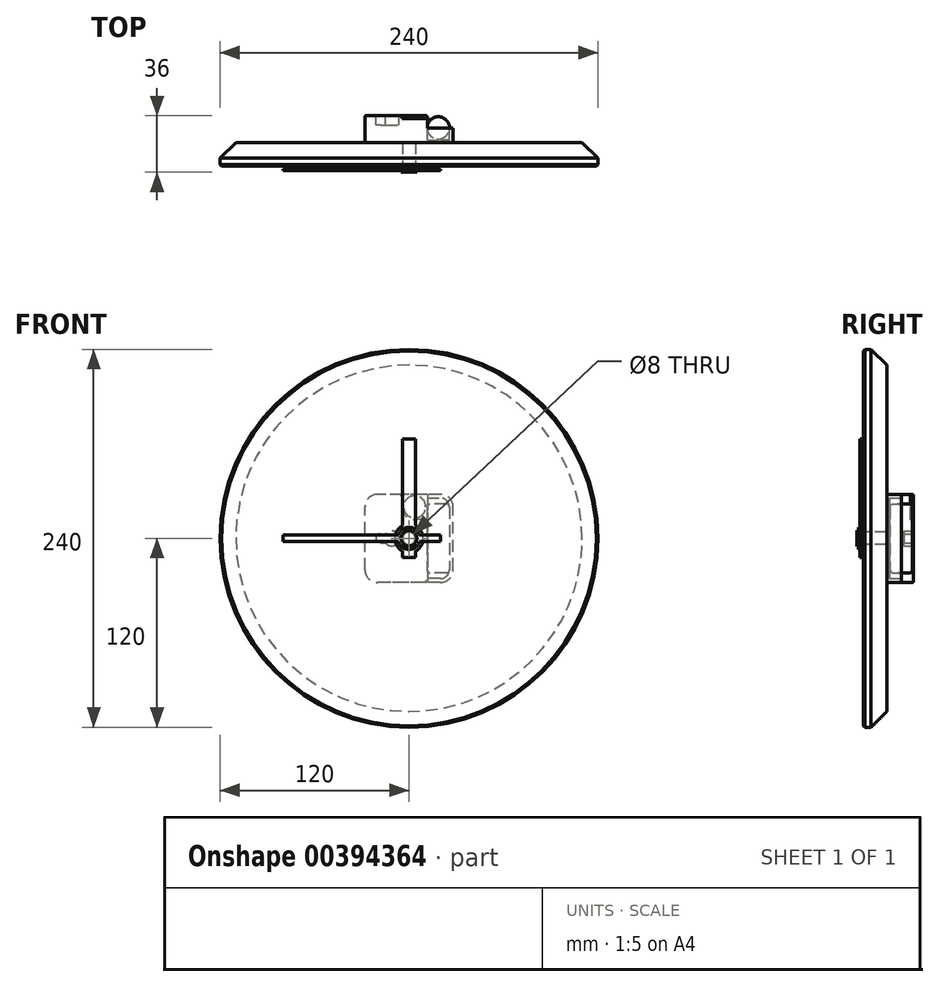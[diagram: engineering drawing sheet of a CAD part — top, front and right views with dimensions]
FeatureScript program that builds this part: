
annotation { "Feature Type Name" : "Feature", "Feature Type Description" : "" }
export const myFeature = defineFeature(function(context is Context, id is Id, definition is map)
    precondition{}
    {
        {
            var Q0;
            Q0=qCreatedBy(makeId("Front.planeOp"),FACE);
            var sketch = newSketch(context, id + "F0", { "sketchPlane" : qUnion([Q0])});
            skCircle(sketch, "E0", {"center": v(0, 0) * mm, "radius": 120 * mm});
            skSolve(sketch);
        }
        {
            var Q0;
            Q0=makeQuery(id+"F0.imprint","IMPRINT",FACE,{"disambiguationData":[TD([[makeQuery(id+"F0.imprint","IMPRINT",EDGE,{"derivedFrom":sQuery(id+"F0.wireOp",EDGE,"E0")}),1.0]])]});
            extrude(context, id + "F1", {"entities" : qUnion([Q0]), "oppositeDirection" : true, "depth" : 15 * mm});
        }
        {
            var Q0;
            Q0=makeQuery(id+"F1.opExtrude","CAP_FACE",FACE,{"disambiguationData":[OSD([sQuery(id+"F0.wireOp",EDGE,"E0")])],"isStart":false});
            var sketch = newSketch(context, id + "F2", { "sketchPlane" : qUnion([Q0])});
            skCircle(sketch, "E1", {"center": v(0, 0) * mm, "radius": 2.5 * mm});
            skSolve(sketch);
        }
        {
            var Q0;
            Q0=makeQuery(id+"F2.imprint","IMPRINT",FACE,{"disambiguationData":[TD([[makeQuery(id+"F2.imprint","IMPRINT",EDGE,{"derivedFrom":sQuery(id+"F2.wireOp",EDGE,"E1")}),1.0]])]});
            var Q1;
            Q1=makeQuery(id+"F1.opExtrude","CAP_FACE",FACE,{"disambiguationData":[OSD([sQuery(id+"F0.wireOp",EDGE,"E0")])],"isStart":true});
            extrude(context, id + "F3", {"entities" : qUnion([Q0]), "operationType" : NewBodyOperationType.REMOVE, "endBound" : BoundingType.UP_TO_SURFACE, "oppositeDirection" : true, "endBoundEntityFace" : qUnion([Q1]), "depth" : 20 * mm});
        }
        {
            var Q0;
            Q0=makeQuery(id+"F1.opExtrude","CAP_FACE",FACE,{"disambiguationData":[OSD([sQuery(id+"F0.wireOp",EDGE,"E0")])],"isStart":false});
            var sketch = newSketch(context, id + "F4", { "sketchPlane" : qUnion([Q0])});
            skLineSegment(sketch, "E2.bottom", {"start": v(-20, -28) * mm, "end": v(20, -28) * mm});
            skLineSegment(sketch, "E2.top", {"start": v(-20, 28) * mm, "end": v(20, 28) * mm});
            skLineSegment(sketch, "E2.left", {"start": v(-28, -20) * mm, "end": v(-28, 20) * mm});
            skLineSegment(sketch, "E2.right", {"start": v(28, -20) * mm, "end": v(28, 20) * mm});
            skPoint(sketch, "E2.middle", {"position": v(0, 0) * mm});
            skPoint(sketch, "E3.visualSharp", {"position": v(28, 28) * mm});
            skArc(sketch, "E3.filletArc", {"start": v(28, 20) * mm, "mid": v(25.66, 25.66) * mm, "end": v(20, 28) * mm});
            skPoint(sketch, "E4.visualSharp", {"position": v(-28, 28) * mm});
            skArc(sketch, "E4.filletArc", {"start": v(-20, 28) * mm, "mid": v(-25.66, 25.66) * mm, "end": v(-28, 20) * mm});
            skPoint(sketch, "E5.visualSharp", {"position": v(-28, -28) * mm});
            skArc(sketch, "E5.filletArc", {"start": v(-28, -20) * mm, "mid": v(-25.66, -25.66) * mm, "end": v(-20, -28) * mm});
            skPoint(sketch, "E6.visualSharp", {"position": v(28, -28) * mm});
            skArc(sketch, "E6.filletArc", {"start": v(20, -28) * mm, "mid": v(25.66, -25.66) * mm, "end": v(28, -20) * mm});
            skSolve(sketch);
        }
        {
            var Q0;
            Q0 = qSketchRegion(id + "F4", true);
            extrude(context, id + "F5", {"entities" : qUnion([Q0]), "depth" : 17 * mm});
        }
        {
            var Q0;
            Q0=makeQuery(id+"F5.opExtrude","CAP_FACE",FACE,{"disambiguationData":[OSD([sQuery(id+"F4.wireOp",EDGE,"E2.bottom"),sQuery(id+"F4.wireOp",EDGE,"E2.top"),sQuery(id+"F4.wireOp",EDGE,"E2.left"),sQuery(id+"F4.wireOp",EDGE,"E2.right"),sQuery(id+"F4.wireOp",EDGE,"E3.filletArc"),sQuery(id+"F4.wireOp",EDGE,"E4.filletArc"),sQuery(id+"F4.wireOp",EDGE,"E5.filletArc"),sQuery(id+"F4.wireOp",EDGE,"E6.filletArc")])],"isStart":false});
            var sketch = newSketch(context, id + "F6", { "sketchPlane" : qUnion([Q0])});
            skArc(sketch, "E7.0", {"start": v(-25.6, -20) * mm, "mid": v(-23.96, -23.96) * mm, "end": v(-20, -25.6) * mm});
            skLineSegment(sketch, "E7.1", {"start": v(-25.6, -20) * mm, "end": v(-25.6, 20) * mm});
            skArc(sketch, "E7.2", {"start": v(-20, 25.6) * mm, "mid": v(-23.96, 23.96) * mm, "end": v(-25.6, 20) * mm});
            skLineSegment(sketch, "E8", {"start": v(-20, 25.6) * mm, "end": v(-11.6, 25.6) * mm});
            skLineSegment(sketch, "E9", {"start": v(-11.6, 25.6) * mm, "end": v(-11.6, -25.6) * mm});
            skLineSegment(sketch, "E10", {"start": v(-11.6, -25.6) * mm, "end": v(-20, -25.6) * mm});
            skSolve(sketch);
        }
        {
            var Q0;
            Q0 = qSketchRegion(id + "F6", true);
            extrude(context, id + "F7", {"entities" : qUnion([Q0]), "operationType" : NewBodyOperationType.REMOVE, "oppositeDirection" : true, "depth" : 15.5 * mm});
        }
        {
            var Q0;
            Q0=makeQuery(id+"F5.opExtrude","CAP_FACE",FACE,{"disambiguationData":[OSD([sQuery(id+"F4.wireOp",EDGE,"E2.bottom"),sQuery(id+"F4.wireOp",EDGE,"E2.top"),sQuery(id+"F4.wireOp",EDGE,"E2.left"),sQuery(id+"F4.wireOp",EDGE,"E2.right"),sQuery(id+"F4.wireOp",EDGE,"E3.filletArc"),sQuery(id+"F4.wireOp",EDGE,"E4.filletArc"),sQuery(id+"F4.wireOp",EDGE,"E5.filletArc"),sQuery(id+"F4.wireOp",EDGE,"E6.filletArc")])],"isStart":false});
            var sketch = newSketch(context, id + "F8", { "sketchPlane" : qUnion([Q0])});
            skLineSegment(sketch, "E11.bottom", {"start": v(-28, -28) * mm, "end": v(-11.6, -28) * mm});
            skLineSegment(sketch, "E11.top", {"start": v(-28, 28) * mm, "end": v(-11.6, 28) * mm});
            skLineSegment(sketch, "E11.left", {"start": v(-28, -28) * mm, "end": v(-28, 28) * mm});
            skLineSegment(sketch, "E11.right", {"start": v(-11.6, -28) * mm, "end": v(-11.6, 28) * mm});
            skSolve(sketch);
        }
        {
            var Q0;
            Q0 = qSketchRegion(id + "F8", true);
            extrude(context, id + "F9", {"entities" : qUnion([Q0]), "operationType" : NewBodyOperationType.REMOVE, "oppositeDirection" : true, "depth" : 7.8 * mm});
        }
        {
            var Q0;
            Q0=makeQuery(id+"F5.opExtrude","CAP_FACE",FACE,{"disambiguationData":[OSD([sQuery(id+"F4.wireOp",EDGE,"E2.bottom"),sQuery(id+"F4.wireOp",EDGE,"E2.top"),sQuery(id+"F4.wireOp",EDGE,"E2.left"),sQuery(id+"F4.wireOp",EDGE,"E2.right"),sQuery(id+"F4.wireOp",EDGE,"E3.filletArc"),sQuery(id+"F4.wireOp",EDGE,"E4.filletArc"),sQuery(id+"F4.wireOp",EDGE,"E5.filletArc"),sQuery(id+"F4.wireOp",EDGE,"E6.filletArc")])],"isStart":false});
            var sketch = newSketch(context, id + "F10", { "sketchPlane" : qUnion([Q0])});
            skLineSegment(sketch, "E12", {"start": v(-11.6, 12) * mm, "end": v(-3.6, 12) * mm});
            skLineSegment(sketch, "E13", {"start": v(4.4, 28) * mm, "end": v(4.4, 20) * mm});
            skArc(sketch, "E14", {"start": v(-3.6, 12) * mm, "mid": v(2.06, 14.34) * mm, "end": v(4.4, 20) * mm});
            skCircle(sketch, "E15", {"center": v(-3.6, 20) * mm, "radius": 7 * mm});
            skLineSegment(sketch, "E16", {"start": v(-11.6, 12) * mm, "end": v(4.4, 28) * mm, "construction": true});
            skLineSegment(sketch, "E17", {"start": v(-11.6, 12) * mm, "end": v(-11.6, 28) * mm});
            skLineSegment(sketch, "E18", {"start": v(-11.6, 28) * mm, "end": v(4.4, 28) * mm});
            skSolve(sketch);
        }
        {
            var Q0;
            Q0 = qSketchRegion(id + "F10", true);
            extrude(context, id + "F11", {"entities" : qUnion([Q0]), "operationType" : NewBodyOperationType.REMOVE, "oppositeDirection" : true, "depth" : 2 * mm});
        }
        {
            var Q0;
            {var subQ0=sQuery(id+"F4.wireOp",EDGE,"E3.filletArc");var subQ1=sQuery(id+"F4.wireOp",EDGE,"E2.top");var subQ2=sQuery(id+"F4.wireOp",EDGE,"E2.right");var subQ3=sQuery(id+"F4.wireOp",EDGE,"E2.bottom");var subQ4=sQuery(id+"F4.wireOp",EDGE,"E6.filletArc");Q0=makeQuery(id+"F11.boolean.opBoolean","SPLIT",FACE,{"disambiguationData":[TD([makeQuery(id+"F5.opExtrude","SWEPT_FACE",FACE,{"disambiguationData":[OSD([subQ3])]})])],"derivedFrom":makeQuery(id+"F5.opExtrude","CAP_FACE",FACE,{"disambiguationData":[OSD([subQ3,subQ1,sQuery(id+"F4.wireOp",EDGE,"E2.left"),subQ2,subQ0,sQuery(id+"F4.wireOp",EDGE,"E4.filletArc"),sQuery(id+"F4.wireOp",EDGE,"E5.filletArc"),subQ4])],"isStart":false})});}
            var Q1;
            Q1=makeQuery(id+"F5.opExtrude","CAP_FACE",FACE,{"disambiguationData":[OSD([sQuery(id+"F4.wireOp",EDGE,"E2.bottom"),sQuery(id+"F4.wireOp",EDGE,"E2.top"),sQuery(id+"F4.wireOp",EDGE,"E2.left"),sQuery(id+"F4.wireOp",EDGE,"E2.right"),sQuery(id+"F4.wireOp",EDGE,"E3.filletArc"),sQuery(id+"F4.wireOp",EDGE,"E4.filletArc"),sQuery(id+"F4.wireOp",EDGE,"E5.filletArc"),sQuery(id+"F4.wireOp",EDGE,"E6.filletArc")])],"isStart":true});
            fillet(context, id + "F12", {"entities" : qUnion([Q0, Q1]), "radius" : 1 * mm, "tangentPropagation" : true, "allowEdgeOverflow" : false});
        }
        {
            var Q0;
            Q0=qCreatedBy(makeId("Top.planeOp"),FACE);
            var sketch = newSketch(context, id + "F13", { "sketchPlane" : qUnion([Q0])});
            skCircle(sketch, "E19", {"center": v(18.6, 24.2) * mm, "radius": 7.12 * mm});
            skLineSegment(sketch, "E20", {"start": v(25.6, 24.2) * mm, "end": v(11.6, 24.2) * mm, "construction": true});
            skSolve(sketch);
        }
        {
            var Q0;
            Q0 = qSketchRegion(id + "F13", true);
            extrude(context, id + "F14", {"entities" : qUnion([Q0]), "endBound" : BoundingType.SYMMETRIC, "depth" : 43.8 * mm, "hasSecondDirection" : true, "secondDirectionOppositeDirection" : true, "secondDirectionDepth" : 24.2 * mm});
        }
        {
            var Q0;
            Q0=makeQuery(id+"F14.opExtrude","CAP_FACE",FACE,{"disambiguationData":[OSD([sQuery(id+"F13.wireOp",EDGE,"E19")])],"isStart":true});
            var Q1;
            Q1=makeQuery(id+"F14.opExtrude","CAP_FACE",FACE,{"disambiguationData":[OSD([sQuery(id+"F13.wireOp",EDGE,"E19")])],"isStart":false});
            fillet(context, id + "F15", {"entities" : qUnion([Q0, Q1]), "radius" : 2 * mm, "tangentPropagation" : true, "allowEdgeOverflow" : false});
        }
        {
            var Q0;
            Q0=makeQuery(id+"F1.opExtrude","CAP_FACE",FACE,{"disambiguationData":[OSD([sQuery(id+"F0.wireOp",EDGE,"E0")])],"isStart":true});
            var sketch = newSketch(context, id + "F16", { "sketchPlane" : qUnion([Q0])});
            skCircle(sketch, "E21", {"center": v(0, 0) * mm, "radius": 4 * mm});
            skSolve(sketch);
        }
        {
            var Q0;
            Q0 = qSketchRegion(id + "F16", true);
            var Q1;
            Q1=makeQuery(id+"F5.opExtrude","CAP_FACE",FACE,{"disambiguationData":[OSD([sQuery(id+"F4.wireOp",EDGE,"E2.bottom"),sQuery(id+"F4.wireOp",EDGE,"E2.top"),sQuery(id+"F4.wireOp",EDGE,"E2.left"),sQuery(id+"F4.wireOp",EDGE,"E2.right"),sQuery(id+"F4.wireOp",EDGE,"E3.filletArc"),sQuery(id+"F4.wireOp",EDGE,"E4.filletArc"),sQuery(id+"F4.wireOp",EDGE,"E5.filletArc"),sQuery(id+"F4.wireOp",EDGE,"E6.filletArc")])],"isStart":true});
            extrude(context, id + "F17", {"entities" : qUnion([Q0]), "operationType" : NewBodyOperationType.REMOVE, "endBound" : BoundingType.UP_TO_SURFACE, "oppositeDirection" : true, "endBoundEntityFace" : qUnion([Q1]), "depth" : 25 * mm});
        }
        {
            var Q0;
            Q0=makeQuery(id+"F1.opExtrude","CAP_FACE",FACE,{"disambiguationData":[OSD([sQuery(id+"F0.wireOp",EDGE,"E0")])],"isStart":true});
            var sketch = newSketch(context, id + "F18", { "sketchPlane" : qUnion([Q0])});
            skArc(sketch, "E22", {"start": v(-4, -8) * mm, "mid": v(0, -12) * mm, "end": v(4, -8) * mm, "construction": true});
            skArc(sketch, "E23", {"start": v(4, 59) * mm, "mid": v(0, 63) * mm, "end": v(-4, 59) * mm, "construction": true});
            skLineSegment(sketch, "E24", {"start": v(0, -8) * mm, "end": v(0, 59) * mm, "construction": true});
            skLineSegment(sketch, "E25", {"start": v(-4, -8) * mm, "end": v(-4, 59) * mm});
            skLineSegment(sketch, "E26", {"start": v(4, -8) * mm, "end": v(4, 59) * mm});
            skCircle(sketch, "E27", {"center": v(0, 0) * mm, "radius": 9 * mm});
            skLineSegment(sketch, "E28", {"start": v(4, -8) * mm, "end": v(4, -12) * mm});
            skPoint(sketch, "E28.endSnap0", {"position": v(0, -12) * mm});
            skLineSegment(sketch, "E29", {"start": v(4, -12) * mm, "end": v(-4, -12) * mm});
            skLineSegment(sketch, "E30", {"start": v(-4, -12) * mm, "end": v(-4, -8) * mm});
            skLineSegment(sketch, "E31", {"start": v(4, 59) * mm, "end": v(4, 63) * mm});
            skLineSegment(sketch, "E32", {"start": v(4, 63) * mm, "end": v(-4, 63) * mm});
            skLineSegment(sketch, "E33", {"start": v(-4, 63) * mm, "end": v(-4, 59) * mm});
            skSolve(sketch);
        }
        {
            var Q0;
            Q0 = qSketchRegion(id + "F18", true);
            extrude(context, id + "F19", {"entities" : qUnion([Q0]), "depth" : 2 * mm, "hasSecondDirection" : true, "secondDirectionOppositeDirection" : false, "secondDirectionDepth" : 1 * mm});
        }
        {
            var Q0;
            Q0=makeQuery(id+"F19.opExtrude","CAP_FACE",FACE,{"disambiguationData":[OSD([sQuery(id+"F18.wireOp",EDGE,"E22"),sQuery(id+"F18.wireOp",EDGE,"E23"),sQuery(id+"F18.wireOp",EDGE,"E25"),sQuery(id+"F18.wireOp",EDGE,"E26")])],"isStart":false});
            var sketch = newSketch(context, id + "F20", { "sketchPlane" : qUnion([Q0])});
            skCircle(sketch, "E34", {"center": v(0, 0) * mm, "radius": 7 * mm});
            skLineSegment(sketch, "E35.bottom", {"start": v(20, -2) * mm, "end": v(-80, -2) * mm});
            skLineSegment(sketch, "E35.top", {"start": v(20, 2) * mm, "end": v(-80, 2) * mm});
            skLineSegment(sketch, "E35.left", {"start": v(20, -2) * mm, "end": v(20, 2) * mm});
            skLineSegment(sketch, "E35.right", {"start": v(-80, -2) * mm, "end": v(-80, 2) * mm});
            skLineSegment(sketch, "E36", {"start": v(-80, 0) * mm, "end": v(20, 0) * mm, "construction": true});
            skSolve(sketch);
        }
        {
            var Q0;
            Q0 = qSketchRegion(id + "F20", true);
            extrude(context, id + "F21", {"entities" : qUnion([Q0]), "depth" : 1 * mm});
        }
        {
            var Q0;
            Q0=makeQuery(id+"F21.opExtrude","CAP_FACE",FACE,{"disambiguationData":[OSD([sQuery(id+"F20.wireOp",EDGE,"E34"),sQuery(id+"F20.wireOp",EDGE,"E35.bottom"),sQuery(id+"F20.wireOp",EDGE,"E35.top"),sQuery(id+"F20.wireOp",EDGE,"E35.left"),sQuery(id+"F20.wireOp",EDGE,"E35.right")])],"isStart":false});
            var sketch = newSketch(context, id + "F22", { "sketchPlane" : qUnion([Q0])});
            skPoint(sketch, "E37", {"position": v(0, 0) * mm});
            skCircle(sketch, "E38", {"center": v(0, 0) * mm, "radius": 5 * mm});
            skSolve(sketch);
        }
        {
            var Q0;
            Q0 = qSketchRegion(id + "F22", true);
            extrude(context, id + "F23", {"entities" : qUnion([Q0]), "depth" : 1 * mm});
        }
        {
            var Q0;
            Q0=makeQuery(id+"F1.opExtrude","CAP_EDGE",EDGE,{"disambiguationData":[OSD([sQuery(id+"F0.wireOp",EDGE,"E0")])],"isStart":true});
            chamfer(context, id + "F24", {"entities" : qUnion([Q0]), "width" : 1 * mm, "tangentPropagation" : true});
        }
        {
            var Q0;
            Q0=makeQuery(id+"F1.opExtrude","CAP_EDGE",EDGE,{"disambiguationData":[OSD([sQuery(id+"F0.wireOp",EDGE,"E0")])],"isStart":false});
            chamfer(context, id + "F25", {"entities" : qUnion([Q0]), "width" : 10 * mm, "tangentPropagation" : true});
        }
        {
            var Q0;
            {var subQ0=sQuery(id+"F4.wireOp",EDGE,"E3.filletArc");var subQ1=sQuery(id+"F4.wireOp",EDGE,"E2.top");var subQ2=sQuery(id+"F4.wireOp",EDGE,"E2.right");var subQ3=sQuery(id+"F4.wireOp",EDGE,"E2.bottom");var subQ4=sQuery(id+"F4.wireOp",EDGE,"E6.filletArc");Q0=makeQuery(id+"F11.boolean.opBoolean","SPLIT",FACE,{"disambiguationData":[TD([makeQuery(id+"F5.opExtrude","SWEPT_FACE",FACE,{"disambiguationData":[OSD([subQ3])]})])],"derivedFrom":makeQuery(id+"F5.opExtrude","CAP_FACE",FACE,{"disambiguationData":[OSD([subQ3,subQ1,sQuery(id+"F4.wireOp",EDGE,"E2.left"),subQ2,subQ0,sQuery(id+"F4.wireOp",EDGE,"E4.filletArc"),sQuery(id+"F4.wireOp",EDGE,"E5.filletArc"),subQ4])],"isStart":false})});}
            var sketch = newSketch(context, id + "F26", { "sketchPlane" : qUnion([Q0])});
            skArc(sketch, "E39", {"start": v(18.1, -2.87) * mm, "mid": v(20.97, 0) * mm, "end": v(18.1, 2.87) * mm});
            skArc(sketch, "E40", {"start": v(14.9, 2.87) * mm, "mid": v(6.31, 0) * mm, "end": v(14.9, -2.87) * mm});
            skLineSegment(sketch, "E41", {"start": v(18.1, -2.87) * mm, "end": v(14.9, -2.87) * mm});
            skLineSegment(sketch, "E42", {"start": v(18.1, 2.87) * mm, "end": v(14.9, 2.87) * mm});
            skSolve(sketch);
        }
        {
            var Q0;
            Q0 = qSketchRegion(id + "F26", true);
            extrude(context, id + "F27", {"entities" : qUnion([Q0]), "operationType" : NewBodyOperationType.REMOVE, "oppositeDirection" : true, "depth" : 6 * mm});
        }
    });
